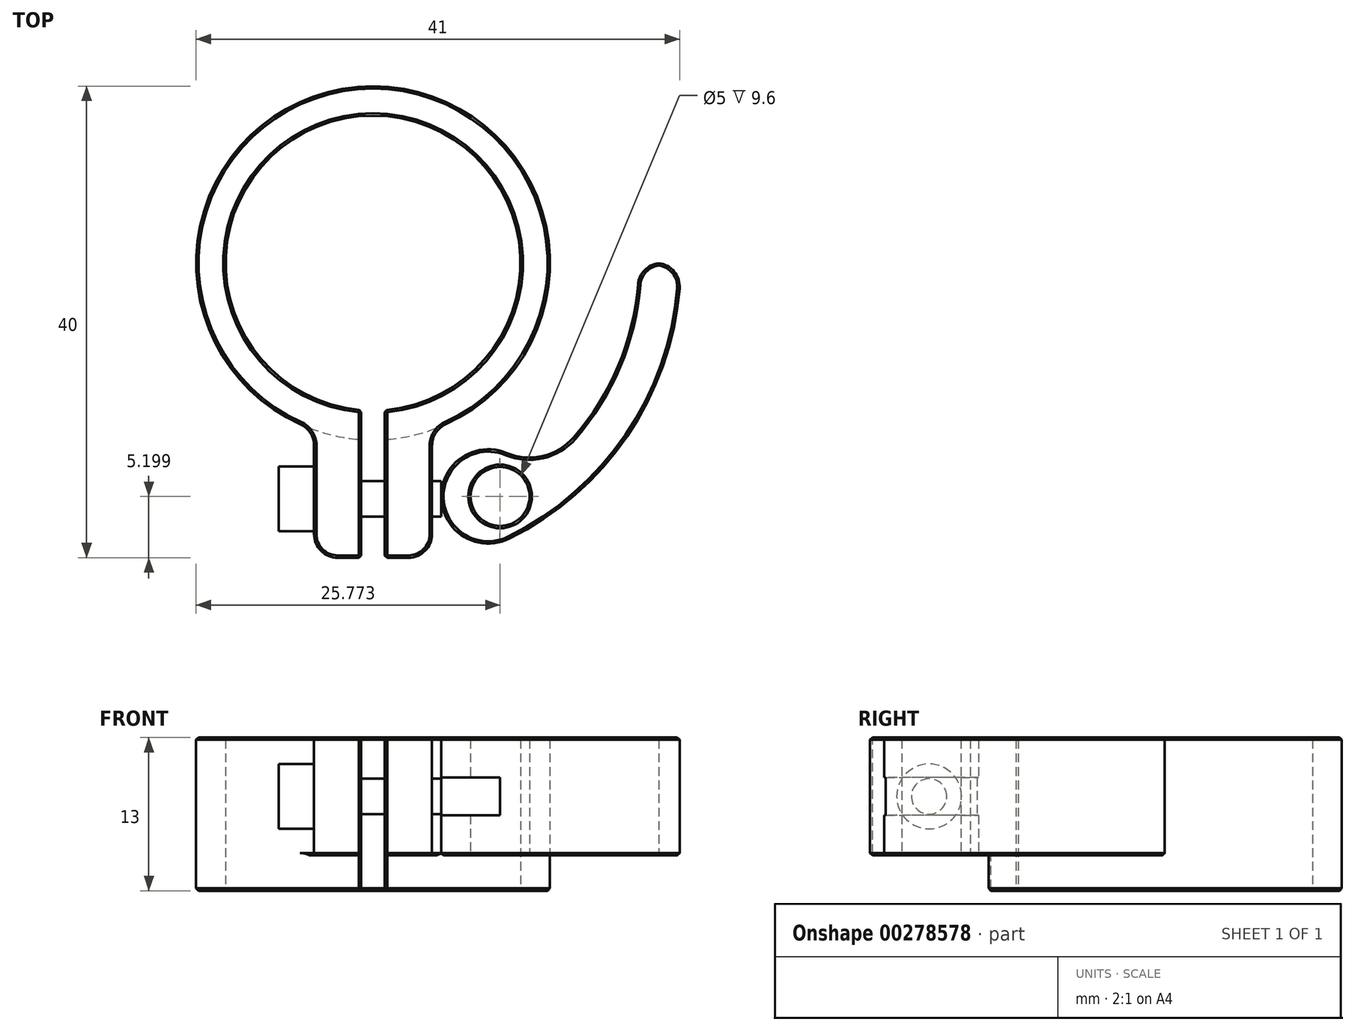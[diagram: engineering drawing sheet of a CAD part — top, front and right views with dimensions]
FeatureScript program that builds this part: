
annotation { "Feature Type Name" : "Feature", "Feature Type Description" : "" }
export const myFeature = defineFeature(function(context is Context, id is Id, definition is map)
    precondition{}
    {
        {
            var Q0;
            Q0=qCreatedBy(makeId("Top.planeOp"),FACE);
            var sketch = newSketch(context, id + "F0", { "sketchPlane" : qUnion([Q0])});
            skCircle(sketch, "E0", {"center": v(0, 0) * mm, "radius": 12.5 * mm});
            skCircle(sketch, "E1", {"center": v(0, 0) * mm, "radius": 15 * mm});
            skLineSegment(sketch, "E2.bottom", {"start": v(5, -25) * mm, "end": v(-5, -25) * mm});
            skLineSegment(sketch, "E2.top", {"start": v(5, 0) * mm, "end": v(-5, 0) * mm});
            skLineSegment(sketch, "E2.left", {"start": v(5, -25) * mm, "end": v(5, 0) * mm});
            skLineSegment(sketch, "E2.right", {"start": v(-5, -25) * mm, "end": v(-5, 0) * mm});
            skPoint(sketch, "E2.middle", {"position": v(0, -12.5) * mm});
            skLineSegment(sketch, "E3.bottom", {"start": v(1, -33.33) * mm, "end": v(-1, -33.33) * mm});
            skLineSegment(sketch, "E3.top", {"start": v(1, 8.32) * mm, "end": v(-1, 8.32) * mm});
            skLineSegment(sketch, "E3.left", {"start": v(1, -33.33) * mm, "end": v(1, 8.32) * mm});
            skLineSegment(sketch, "E3.right", {"start": v(-1, -33.33) * mm, "end": v(-1, 8.32) * mm});
            skSolve(sketch);
        }
        {
            var Q0;
            {var subQ0=sQuery(id+"F0.wireOp",EDGE,"E2.right");var subQ1=sQuery(id+"F0.wireOp",EDGE,"E0");var subQ2=makeQuery(id+"F0.imprint","INTERSECT",VERTEX,{"derivedFrom":[subQ1,subQ0]});Q0=makeQuery(id+"F0.imprint","IMPRINT",FACE,{"disambiguationData":[TD([[makeQuery(id+"F0.imprint","IMPRINT",EDGE,{"disambiguationData":[TD([[subQ2,1.0]])],"derivedFrom":subQ1}),-1.0]])]});}
            var Q1;
            {var subQ0=sQuery(id+"F0.wireOp",EDGE,"E2.left");var subQ1=sQuery(id+"F0.wireOp",EDGE,"E1");var subQ2=makeQuery(id+"F0.imprint","INTERSECT",VERTEX,{"derivedFrom":[subQ1,subQ0]});Q1=makeQuery(id+"F0.imprint","IMPRINT",FACE,{"disambiguationData":[TD([[makeQuery(id+"F0.imprint","IMPRINT",EDGE,{"disambiguationData":[TD([[subQ2,1.0]])],"derivedFrom":subQ1}),-1.0]])]});}
            var Q2;
            {var subQ0=sQuery(id+"F0.wireOp",EDGE,"E2.right");var subQ1=sQuery(id+"F0.wireOp",EDGE,"E1");var subQ2=makeQuery(id+"F0.imprint","INTERSECT",VERTEX,{"derivedFrom":[subQ1,subQ0]});Q2=makeQuery(id+"F0.imprint","IMPRINT",FACE,{"disambiguationData":[TD([[makeQuery(id+"F0.imprint","IMPRINT",EDGE,{"disambiguationData":[TD([[subQ2,-1.0]])],"derivedFrom":subQ1}),-1.0]])]});}
            var Q3;
            {var subQ0=sQuery(id+"F0.wireOp",EDGE,"E3.right");var subQ1=sQuery(id+"F0.wireOp",EDGE,"E0");var subQ2=makeQuery(id+"F0.imprint","INTERSECT",VERTEX,{"derivedFrom":[subQ1,subQ0]});Q3=makeQuery(id+"F0.imprint","IMPRINT",FACE,{"disambiguationData":[TD([[makeQuery(id+"F0.imprint","IMPRINT",EDGE,{"disambiguationData":[TD([[subQ2,1.0]])],"derivedFrom":subQ1}),-1.0]])]});}
            var Q4;
            {var subQ0=sQuery(id+"F0.wireOp",EDGE,"E3.left");var subQ1=sQuery(id+"F0.wireOp",EDGE,"E0");var subQ2=makeQuery(id+"F0.imprint","INTERSECT",VERTEX,{"derivedFrom":[subQ1,subQ0]});Q4=makeQuery(id+"F0.imprint","IMPRINT",FACE,{"disambiguationData":[TD([[makeQuery(id+"F0.imprint","IMPRINT",EDGE,{"disambiguationData":[TD([[subQ2,-1.0]])],"derivedFrom":subQ1}),-1.0]])]});}
            extrude(context, id + "F1", {"entities" : qUnion([Q0, Q1, Q2, Q3, Q4]), "depth" : 5 * mm, "hasSecondDirection" : true, "secondDirectionOppositeDirection" : true, "secondDirectionDepth" : 5 * mm});
        }
        {
            var Q0;
            {var subQ0=sQuery(id+"F0.wireOp",EDGE,"E2.right");var subQ1=sQuery(id+"F0.wireOp",EDGE,"E0");var subQ2=makeQuery(id+"F0.imprint","INTERSECT",VERTEX,{"derivedFrom":[subQ1,subQ0]});Q0=makeQuery(id+"F0.imprint","IMPRINT",FACE,{"disambiguationData":[TD([[makeQuery(id+"F0.imprint","IMPRINT",EDGE,{"disambiguationData":[TD([[subQ2,1.0]])],"derivedFrom":subQ1}),-1.0]])]});}
            var Q1;
            Q1=makeQuery(id+"F1.opExtrude","CAP_FACE",FACE,{"disambiguationData":[OSD([sQuery(id+"F0.wireOp",EDGE,"E0"),sQuery(id+"F0.wireOp",EDGE,"E1"),sQuery(id+"F0.wireOp",EDGE,"E2.bottom"),sQuery(id+"F0.wireOp",EDGE,"E2.left"),sQuery(id+"F0.wireOp",EDGE,"E2.right"),sQuery(id+"F0.wireOp",EDGE,"E3.left"),sQuery(id+"F0.wireOp",EDGE,"E3.right")])],"isStart":false});
            var Q2;
            {var subQ0=sQuery(id+"F0.wireOp",EDGE,"E3.right");var subQ1=sQuery(id+"F0.wireOp",EDGE,"E0");var subQ2=makeQuery(id+"F0.imprint","INTERSECT",VERTEX,{"derivedFrom":[subQ1,subQ0]});Q2=makeQuery(id+"F0.imprint","IMPRINT",FACE,{"disambiguationData":[TD([[makeQuery(id+"F0.imprint","IMPRINT",EDGE,{"disambiguationData":[TD([[subQ2,1.0]])],"derivedFrom":subQ1}),-1.0]])]});}
            var Q3;
            {var subQ0=sQuery(id+"F0.wireOp",EDGE,"E3.left");var subQ1=sQuery(id+"F0.wireOp",EDGE,"E0");var subQ2=makeQuery(id+"F0.imprint","INTERSECT",VERTEX,{"derivedFrom":[subQ1,subQ0]});Q3=makeQuery(id+"F0.imprint","IMPRINT",FACE,{"disambiguationData":[TD([[makeQuery(id+"F0.imprint","IMPRINT",EDGE,{"disambiguationData":[TD([[subQ2,-1.0]])],"derivedFrom":subQ1}),-1.0]])]});}
            extrude(context, id + "F2", {"entities" : qUnion([Q0, Q1, Q2, Q3]), "operationType" : NewBodyOperationType.ADD, "depth" : -8 * mm});
        }
        {
            var Q0;
            Q0=makeQuery(id+"F1.opExtrude","SWEPT_EDGE",EDGE,{"disambiguationData":[OSD([sQuery(id+"F0.wireOp",EDGE,"E1"),sQuery(id+"F0.wireOp",EDGE,"E2.right")])]});
            var Q1;
            Q1=makeQuery(id+"F1.opExtrude","SWEPT_EDGE",EDGE,{"disambiguationData":[OSD([sQuery(id+"F0.wireOp",EDGE,"E1"),sQuery(id+"F0.wireOp",EDGE,"E2.left")])]});
            var Q2;
            Q2=makeQuery(id+"F1.opExtrude","SWEPT_EDGE",EDGE,{"disambiguationData":[OSD([sQuery(id+"F0.wireOp",EDGE,"E2.bottom"),sQuery(id+"F0.wireOp",EDGE,"E2.right")])]});
            var Q3;
            Q3=makeQuery(id+"F1.opExtrude","SWEPT_EDGE",EDGE,{"disambiguationData":[OSD([sQuery(id+"F0.wireOp",EDGE,"E2.bottom"),sQuery(id+"F0.wireOp",EDGE,"E2.left")])]});
            fillet(context, id + "F3", {"entities" : qUnion([Q0, Q1, Q2, Q3]), "radius" : 2 * mm, "tangentPropagation" : true, "allowEdgeOverflow" : false});
        }
        {
            var Q0;
            Q0=makeQuery(id+"F1.opExtrude","CAP_EDGE",EDGE,{"disambiguationData":[OSD([sQuery(id+"F0.wireOp",EDGE,"E0")])],"isStart":false});
            var Q1;
            Q1=makeQuery(id+"F1.opExtrude","CAP_EDGE",EDGE,{"disambiguationData":[OSD([sQuery(id+"F0.wireOp",EDGE,"E1")])],"isStart":false});
            var Q2;
            Q2=makeQuery(id+"F1.opExtrude","CAP_EDGE",EDGE,{"disambiguationData":[OSD([sQuery(id+"F0.wireOp",EDGE,"E2.right")])],"isStart":false});
            var Q3;
            Q3=makeQuery(id+"F1.opExtrude","CAP_EDGE",EDGE,{"disambiguationData":[OSD([sQuery(id+"F0.wireOp",EDGE,"E2.left")])],"isStart":false});
            var Q4;
            Q4=makeQuery(id+"F1.opExtrude","CAP_EDGE",EDGE,{"disambiguationData":[OSD([sQuery(id+"F0.wireOp",EDGE,"E3.right")])],"isStart":false});
            var Q5;
            Q5=makeQuery(id+"F1.opExtrude","CAP_EDGE",EDGE,{"disambiguationData":[OSD([sQuery(id+"F0.wireOp",EDGE,"E3.left")])],"isStart":false});
            var Q6;
            {var subQ0=sQuery(id+"F0.wireOp",EDGE,"E3.left");var subQ1=sQuery(id+"F0.wireOp",EDGE,"E0");Q6=makeQuery(id+"F2.boolean.opBoolean","MERGE",EDGE,{"derivedFrom":[makeQuery(id+"F1.opExtrude","SWEPT_EDGE",EDGE,{"disambiguationData":[OSD([subQ1,subQ0])]}),makeQuery(id+"F2.opExtrude","SWEPT_EDGE",EDGE,{"disambiguationData":[OSD([subQ1,subQ0]),TDD([makeQuery(id+"F0.imprint","INTERSECT",VERTEX,{"derivedFrom":[subQ1,subQ0]})])]}),makeQuery(id+"F2.opExtrude","SWEPT_EDGE",EDGE,{"disambiguationData":[OSD([subQ1,subQ0]),TDD([makeQuery(id+"F1.opExtrude","CAP_VERTEX",VERTEX,{"disambiguationData":[OSD([subQ1,subQ0])],"isStart":false})])]})]});}
            var Q7;
            {var subQ0=sQuery(id+"F0.wireOp",EDGE,"E0");var subQ1=makeQuery(id+"F0.imprint","INTERSECT",VERTEX,{"derivedFrom":[subQ0,sQuery(id+"F0.wireOp",EDGE,"E2.right")]});Q7=makeQuery(id+"F2.boolean.opBoolean","MERGE",FACE,{"derivedFrom":[makeQuery(id+"F1.opExtrude","SWEPT_FACE",FACE,{"disambiguationData":[OSD([subQ0])]}),makeQuery(id+"F2.opExtrude","SWEPT_FACE",FACE,{"disambiguationData":[OSD([subQ0]),TDD([makeQuery(id+"F0.imprint","IMPRINT",EDGE,{"disambiguationData":[TD([[makeQuery(id+"F0.imprint","INTERSECT",VERTEX,{"derivedFrom":[subQ0,sQuery(id+"F0.wireOp",EDGE,"E3.right")]}),1.0]])],"derivedFrom":subQ0}),makeQuery(id+"F0.imprint","IMPRINT",EDGE,{"disambiguationData":[TD([[makeQuery(id+"F0.imprint","INTERSECT",VERTEX,{"derivedFrom":[subQ0,sQuery(id+"F0.wireOp",EDGE,"E3.left")]}),-1.0]])],"derivedFrom":subQ0}),makeQuery(id+"F0.imprint","IMPRINT",EDGE,{"disambiguationData":[TD([[subQ1,1.0]])],"derivedFrom":subQ0})])]}),makeQuery(id+"F2.opExtrude","SWEPT_FACE",FACE,{"disambiguationData":[OSD([subQ0]),TDD([makeQuery(id+"F1.opExtrude","CAP_EDGE",EDGE,{"disambiguationData":[OSD([subQ0])],"isStart":false})])]})]});}
            var Q8;
            Q8=makeQuery(id+"F1.opExtrude","CAP_EDGE",EDGE,{"disambiguationData":[OSD([sQuery(id+"F0.wireOp",EDGE,"E3.left")])],"isStart":true});
            var Q9;
            Q9=makeQuery(id+"F1.opExtrude","SWEPT_EDGE",EDGE,{"disambiguationData":[OSD([sQuery(id+"F0.wireOp",EDGE,"E2.bottom"),sQuery(id+"F0.wireOp",EDGE,"E3.left")])]});
            var Q10;
            Q10=makeQuery(id+"F1.opExtrude","SWEPT_EDGE",EDGE,{"disambiguationData":[OSD([sQuery(id+"F0.wireOp",EDGE,"E2.bottom"),sQuery(id+"F0.wireOp",EDGE,"E3.right")])]});
            var Q11;
            Q11=makeQuery(id+"F1.opExtrude","CAP_EDGE",EDGE,{"disambiguationData":[OSD([sQuery(id+"F0.wireOp",EDGE,"E3.right")])],"isStart":true});
            var Q12;
            {var subQ0=sQuery(id+"F0.wireOp",EDGE,"E1");var subQ1=makeQuery(id+"F0.imprint","INTERSECT",VERTEX,{"derivedFrom":[subQ0,sQuery(id+"F0.wireOp",EDGE,"E2.right")]});var subQ2=makeQuery(id+"F0.imprint","INTERSECT",VERTEX,{"derivedFrom":[subQ0,sQuery(id+"F0.wireOp",EDGE,"E2.left")]});Q12=makeQuery(id+"F2.opExtrude","CAP_EDGE",EDGE,{"disambiguationData":[OSD([subQ0]),TDD([makeQuery(id+"F0.imprint","IMPRINT",EDGE,{"disambiguationData":[TD([[subQ1,-1.0]])],"derivedFrom":subQ0}),makeQuery(id+"F0.imprint","IMPRINT",EDGE,{"disambiguationData":[TD([[subQ2,1.0]])],"derivedFrom":subQ0}),makeQuery(id+"F0.imprint","IMPRINT",EDGE,{"disambiguationData":[TD([[subQ1,1.0]])],"derivedFrom":subQ0})])],"isStart":false});}
            var Q13;
            Q13=makeQuery(id+"F2.opExtrude","SWEPT_EDGE",EDGE,{"disambiguationData":[OSD([sQuery(id+"F0.wireOp",EDGE,"E1"),sQuery(id+"F0.wireOp",EDGE,"E3.left")])]});
            var Q14;
            Q14=makeQuery(id+"F2.opExtrude","SWEPT_EDGE",EDGE,{"disambiguationData":[OSD([sQuery(id+"F0.wireOp",EDGE,"E1"),sQuery(id+"F0.wireOp",EDGE,"E3.right")])]});
            var Q15;
            {var subQ0=sQuery(id+"F0.wireOp",EDGE,"E3.left");Q15=makeQuery(id+"F2.opExtrude","CAP_EDGE",EDGE,{"disambiguationData":[OSD([subQ0]),TDD([makeQuery(id+"F0.imprint","IMPRINT",EDGE,{"disambiguationData":[TD([[makeQuery(id+"F0.imprint","INTERSECT",VERTEX,{"derivedFrom":[sQuery(id+"F0.wireOp",EDGE,"E0"),subQ0]}),1.0]])],"derivedFrom":subQ0})])],"isStart":false});}
            var Q16;
            {var subQ0=sQuery(id+"F0.wireOp",EDGE,"E3.right");Q16=makeQuery(id+"F2.opExtrude","CAP_EDGE",EDGE,{"disambiguationData":[OSD([subQ0]),TDD([makeQuery(id+"F0.imprint","IMPRINT",EDGE,{"disambiguationData":[TD([[makeQuery(id+"F0.imprint","INTERSECT",VERTEX,{"derivedFrom":[sQuery(id+"F0.wireOp",EDGE,"E0"),subQ0]}),1.0]])],"derivedFrom":subQ0})])],"isStart":false});}
            var Q17;
            Q17=makeQuery(id+"F1.opExtrude","CAP_EDGE",EDGE,{"disambiguationData":[OSD([sQuery(id+"F0.wireOp",EDGE,"E2.right")])],"isStart":true});
            var Q18;
            Q18=makeQuery(id+"F1.opExtrude","CAP_EDGE",EDGE,{"disambiguationData":[OSD([sQuery(id+"F0.wireOp",EDGE,"E2.left")])],"isStart":true});
            chamfer(context, id + "F4", {"entities" : qUnion([Q0, Q1, Q2, Q3, Q4, Q5, Q6, Q7, Q8, Q9, Q10, Q11, Q12, Q13, Q14, Q15, Q16, Q17, Q18]), "width" : 0.2 * mm, "tangentPropagation" : true});
        }
        {
            var Q0;
            Q0=makeQuery(id+"F1.opExtrude","SWEPT_FACE",FACE,{"disambiguationData":[OSD([sQuery(id+"F0.wireOp",EDGE,"E2.right")])]});
            var sketch = newSketch(context, id + "F5", { "sketchPlane" : qUnion([Q0])});
            skCircle(sketch, "E4", {"center": v(20, 0) * mm, "radius": 1.5 * mm});
            skCircle(sketch, "E5", {"center": v(20, 0) * mm, "radius": 2.75 * mm});
            skSolve(sketch);
        }
        {
            var Q0;
            Q0=makeQuery(id+"F5.imprint","IMPRINT",FACE,{"disambiguationData":[TD([[makeQuery(id+"F5.imprint","IMPRINT",EDGE,{"derivedFrom":sQuery(id+"F5.wireOp",EDGE,"E4")}),1.0]])]});
            extrude(context, id + "F6", {"entities" : qUnion([Q0]), "operationType" : NewBodyOperationType.REMOVE, "oppositeDirection" : true, "depth" : 25 * mm});
        }
        {
            var Q0;
            Q0=makeQuery(id+"F5.imprint","IMPRINT",FACE,{"disambiguationData":[TD([[makeQuery(id+"F5.imprint","IMPRINT",EDGE,{"derivedFrom":sQuery(id+"F5.wireOp",EDGE,"E4")}),-1.0]])]});
            var Q1;
            Q1=makeQuery(id+"F5.imprint","IMPRINT",FACE,{"disambiguationData":[TD([[makeQuery(id+"F5.imprint","IMPRINT",EDGE,{"derivedFrom":sQuery(id+"F5.wireOp",EDGE,"E4")}),1.0]])]});
            extrude(context, id + "F7", {"entities" : qUnion([Q0, Q1]), "depth" : 3 * mm});
        }
        {
            var Q0;
            Q0=makeQuery(id+"F5.imprint","IMPRINT",FACE,{"disambiguationData":[TD([[makeQuery(id+"F5.imprint","IMPRINT",EDGE,{"derivedFrom":sQuery(id+"F5.wireOp",EDGE,"E4")}),1.0]])]});
            extrude(context, id + "F8", {"entities" : qUnion([Q0]), "operationType" : NewBodyOperationType.ADD, "oppositeDirection" : true, "depth" : 14.67 * mm});
        }
        {
            var Q0;
            Q0=qCreatedBy(makeId("Top.planeOp"),FACE);
            var sketch = newSketch(context, id + "F9", { "sketchPlane" : qUnion([Q0])});
            skCircle(sketch, "E6", {"center": v(10.77, -19.8) * mm, "radius": 2.5 * mm});
            skCircle(sketch, "E7", {"center": v(9.77, -19.8) * mm, "radius": 4 * mm});
            skCircle(sketch, "E8", {"center": v(0, 0) * mm, "radius": 26.08 * mm});
            skCircle(sketch, "E9", {"center": v(0, 0) * mm, "radius": 22.54 * mm});
            skLineSegment(sketch, "E10", {"start": v(22.54, 0) * mm, "end": v(26.08, 0) * mm});
            skLineSegment(sketch, "E11.bottom", {"start": v(5.77, -24.1) * mm, "end": v(10.77, -24.1) * mm});
            skLineSegment(sketch, "E11.top", {"start": v(5.77, -14.58) * mm, "end": v(10.77, -14.58) * mm});
            skLineSegment(sketch, "E11.left", {"start": v(5.77, -24.1) * mm, "end": v(5.77, -14.58) * mm});
            skLineSegment(sketch, "E11.right", {"start": v(10.77, -24.1) * mm, "end": v(10.77, -14.58) * mm});
            skSolve(sketch);
        }
        {
            var Q0;
            {var subQ2=sQuery(id+"F9.wireOp",EDGE,"E9");var subQ4=sQuery(id+"F9.wireOp",EDGE,"E6");var subQ5=makeQuery(id+"F9.imprint","INTERSECT",VERTEX,{"disambiguationData":[OD(0.0)],"derivedFrom":[subQ4,subQ2]});Q0=makeQuery(id+"F9.imprint","IMPRINT",FACE,{"disambiguationData":[TD([[makeQuery(id+"F9.imprint","IMPRINT",EDGE,{"disambiguationData":[TD([[subQ5,-1.0]])],"derivedFrom":subQ4}),-1.0]])]});}
            var Q1;
            {var subQ0=sQuery(id+"F9.wireOp",EDGE,"E9");var subQ1=sQuery(id+"F9.wireOp",EDGE,"E6");var subQ2=makeQuery(id+"F9.imprint","INTERSECT",VERTEX,{"disambiguationData":[OD(0.0)],"derivedFrom":[subQ1,subQ0]});Q1=makeQuery(id+"F9.imprint","IMPRINT",FACE,{"disambiguationData":[TD([[makeQuery(id+"F9.imprint","IMPRINT",EDGE,{"disambiguationData":[TD([[subQ2,1.0]])],"derivedFrom":subQ1}),-1.0]])]});}
            var Q2;
            {var subQ5=sQuery(id+"F9.wireOp",EDGE,"E10");Q2=makeQuery(id+"F9.imprint","IMPRINT",FACE,{"disambiguationData":[TD([[makeQuery(id+"F9.imprint","IMPRINT",EDGE,{"derivedFrom":subQ5}),-1.0]])]});}
            var Q3;
            {var subQ0=sQuery(id+"F9.wireOp",EDGE,"9b3e7e2a-e51d-4acb-ae69-ad82b6e70bec.right");var subQ1=sQuery(id+"F9.wireOp",EDGE,"E6");var subQ2=makeQuery(id+"F9.imprint","INTERSECT",VERTEX,{"disambiguationData":[OD(0.0)],"derivedFrom":[subQ1,subQ0]});Q3=makeQuery(id+"F9.imprint","IMPRINT",FACE,{"disambiguationData":[TD([[makeQuery(id+"F9.imprint","IMPRINT",EDGE,{"disambiguationData":[TD([[subQ2,-1.0]])],"derivedFrom":subQ1}),-1.0]])]});}
            var Q4;
            {var subQ5=sQuery(id+"F9.wireOp",EDGE,"E6");var subQ7=sQuery(id+"F9.wireOp",EDGE,"E11.right");var subQ9=makeQuery(id+"F9.imprint","INTERSECT",VERTEX,{"disambiguationData":[OD(0.0)],"derivedFrom":[subQ5,subQ7]});Q4=makeQuery(id+"F9.imprint","IMPRINT",FACE,{"disambiguationData":[TD([[makeQuery(id+"F9.imprint","IMPRINT",EDGE,{"disambiguationData":[TD([[subQ9,-1.0]])],"derivedFrom":subQ5}),-1.0]])]});}
            var Q5;
            {var subQ0=sQuery(id+"F9.wireOp",EDGE,"E9");var subQ1=sQuery(id+"F9.wireOp",EDGE,"E7");var subQ2=makeQuery(id+"F9.imprint","INTERSECT",VERTEX,{"disambiguationData":[OD(1.0)],"derivedFrom":[subQ1,subQ0]});Q5=makeQuery(id+"F9.imprint","IMPRINT",FACE,{"disambiguationData":[TD([[makeQuery(id+"F9.imprint","IMPRINT",EDGE,{"disambiguationData":[TD([[subQ2,-1.0]])],"derivedFrom":subQ1}),1.0]])]});}
            var Q6;
            {var subQ5=sQuery(id+"F9.wireOp",EDGE,"E9");var subQ7=sQuery(id+"F9.wireOp",EDGE,"E6");var subQ8=makeQuery(id+"F9.imprint","INTERSECT",VERTEX,{"disambiguationData":[OD(1.0)],"derivedFrom":[subQ7,subQ5]});Q6=makeQuery(id+"F9.imprint","IMPRINT",FACE,{"disambiguationData":[TD([[makeQuery(id+"F9.imprint","IMPRINT",EDGE,{"disambiguationData":[TD([[subQ8,-1.0]])],"derivedFrom":subQ7}),-1.0]])]});}
            var Q7;
            {var subQ0=sQuery(id+"F9.wireOp",EDGE,"E11.left");var subQ1=sQuery(id+"F9.wireOp",EDGE,"E7");var subQ2=makeQuery(id+"F9.imprint","INTERSECT",VERTEX,{"disambiguationData":[OD(0.0)],"derivedFrom":[subQ1,subQ0]});Q7=makeQuery(id+"F9.imprint","IMPRINT",FACE,{"disambiguationData":[TD([[makeQuery(id+"F9.imprint","IMPRINT",EDGE,{"disambiguationData":[TD([[subQ2,-1.0]])],"derivedFrom":subQ1}),1.0]])]});}
            extrude(context, id + "F10", {"entities" : qUnion([Q0, Q1, Q2, Q3, Q4, Q5, Q6, Q7]), "depth" : 5 * mm, "hasSecondDirection" : true, "secondDirectionOppositeDirection" : true, "secondDirectionDepth" : 5 * mm});
        }
        {
            var Q0;
            Q0=makeQuery(id+"F10.opExtrude","SWEPT_EDGE",EDGE,{"disambiguationData":[OSD([sQuery(id+"F9.wireOp",EDGE,"E9"),sQuery(id+"F9.wireOp",EDGE,"E10")])]});
            var Q1;
            Q1=makeQuery(id+"F10.opExtrude","SWEPT_EDGE",EDGE,{"disambiguationData":[OSD([sQuery(id+"F9.wireOp",EDGE,"E8"),sQuery(id+"F9.wireOp",EDGE,"E10")])]});
            fillet(context, id + "F11", {"entities" : qUnion([Q0, Q1]), "radius" : 2 * mm, "tangentPropagation" : true, "allowEdgeOverflow" : false});
        }
        {
            var Q0;
            Q0=makeQuery(id+"F10.opExtrude","SWEPT_EDGE",EDGE,{"disambiguationData":[OSD([sQuery(id+"F9.wireOp",EDGE,"E7"),sQuery(id+"F9.wireOp",EDGE,"E9")])]});
            fillet(context, id + "F12", {"entities" : qUnion([Q0]), "radius" : 5 * mm, "tangentPropagation" : true, "allowEdgeOverflow" : false});
        }
        {
            var Q0;
            Q0=makeQuery(id+"F10.opExtrude","CAP_EDGE",EDGE,{"disambiguationData":[OSD([sQuery(id+"F9.wireOp",EDGE,"E8")])],"isStart":false});
            var Q1;
            Q1=makeQuery(id+"F10.opExtrude","CAP_EDGE",EDGE,{"disambiguationData":[OSD([sQuery(id+"F9.wireOp",EDGE,"E8")])],"isStart":true});
            var Q2;
            Q2=makeQuery(id+"F10.opExtrude","CAP_FACE",FACE,{"disambiguationData":[OSD([sQuery(id+"F9.wireOp",EDGE,"E6"),sQuery(id+"F9.wireOp",EDGE,"E7"),sQuery(id+"F9.wireOp",EDGE,"E8"),sQuery(id+"F9.wireOp",EDGE,"E9"),sQuery(id+"F9.wireOp",EDGE,"E10")])],"isStart":true});
            var Q3;
            Q3=makeQuery(id+"F10.opExtrude","CAP_EDGE",EDGE,{"disambiguationData":[OSD([sQuery(id+"F9.wireOp",EDGE,"E6")])],"isStart":false});
            chamfer(context, id + "F13", {"entities" : qUnion([Q0, Q1, Q2, Q3]), "width" : 0.2 * mm, "tangentPropagation" : true});
        }
        {
            var Q0;
            {var subQ5=sQuery(id+"F9.wireOp",EDGE,"E9");var subQ7=sQuery(id+"F9.wireOp",EDGE,"E6");var subQ8=makeQuery(id+"F9.imprint","INTERSECT",VERTEX,{"disambiguationData":[OD(1.0)],"derivedFrom":[subQ7,subQ5]});Q0=makeQuery(id+"F9.imprint","IMPRINT",FACE,{"disambiguationData":[TD([[makeQuery(id+"F9.imprint","IMPRINT",EDGE,{"disambiguationData":[TD([[subQ8,-1.0]])],"derivedFrom":subQ7}),-1.0]])]});}
            var Q1;
            {var subQ0=sQuery(id+"F9.wireOp",EDGE,"E9");var subQ1=sQuery(id+"F9.wireOp",EDGE,"E6");var subQ2=makeQuery(id+"F9.imprint","INTERSECT",VERTEX,{"disambiguationData":[OD(1.0)],"derivedFrom":[subQ1,subQ0]});Q1=makeQuery(id+"F9.imprint","IMPRINT",FACE,{"disambiguationData":[TD([[makeQuery(id+"F9.imprint","IMPRINT",EDGE,{"disambiguationData":[TD([[subQ2,-1.0]])],"derivedFrom":subQ1}),1.0]])]});}
            var Q2;
            {var subQ0=sQuery(id+"F9.wireOp",EDGE,"E11.right");var subQ1=sQuery(id+"F9.wireOp",EDGE,"E6");var subQ2=makeQuery(id+"F9.imprint","INTERSECT",VERTEX,{"disambiguationData":[OD(0.0)],"derivedFrom":[subQ1,subQ0]});Q2=makeQuery(id+"F9.imprint","IMPRINT",FACE,{"disambiguationData":[TD([[makeQuery(id+"F9.imprint","IMPRINT",EDGE,{"disambiguationData":[TD([[subQ2,-1.0]])],"derivedFrom":subQ1}),1.0]])]});}
            var Q3;
            {var subQ5=sQuery(id+"F9.wireOp",EDGE,"E6");var subQ7=sQuery(id+"F9.wireOp",EDGE,"E11.right");var subQ9=makeQuery(id+"F9.imprint","INTERSECT",VERTEX,{"disambiguationData":[OD(0.0)],"derivedFrom":[subQ5,subQ7]});Q3=makeQuery(id+"F9.imprint","IMPRINT",FACE,{"disambiguationData":[TD([[makeQuery(id+"F9.imprint","IMPRINT",EDGE,{"disambiguationData":[TD([[subQ9,-1.0]])],"derivedFrom":subQ5}),-1.0]])]});}
            var Q4;
            {var subQ0=sQuery(id+"F9.wireOp",EDGE,"E11.left");var subQ3=sQuery(id+"F9.wireOp",EDGE,"E7");var subQ4=makeQuery(id+"F9.imprint","INTERSECT",VERTEX,{"disambiguationData":[OD(1.0)],"derivedFrom":[subQ3,subQ0]});Q4=makeQuery(id+"F9.imprint","IMPRINT",FACE,{"disambiguationData":[TD([[makeQuery(id+"F9.imprint","IMPRINT",EDGE,{"disambiguationData":[TD([[subQ4,-1.0]])],"derivedFrom":subQ3}),-1.0]])]});}
            var Q5;
            {var subQ0=sQuery(id+"F9.wireOp",EDGE,"E11.bottom");var subQ1=sQuery(id+"F9.wireOp",EDGE,"E8");var subQ2=makeQuery(id+"F9.imprint","INTERSECT",VERTEX,{"derivedFrom":[subQ1,subQ0]});Q5=makeQuery(id+"F9.imprint","IMPRINT",FACE,{"disambiguationData":[TD([[makeQuery(id+"F9.imprint","IMPRINT",EDGE,{"disambiguationData":[TD([[subQ2,-1.0]])],"derivedFrom":subQ1}),-1.0]])]});}
            var Q6;
            {var subQ5=sQuery(id+"F9.wireOp",EDGE,"E11.top");Q6=makeQuery(id+"F9.imprint","IMPRINT",FACE,{"disambiguationData":[TD([[makeQuery(id+"F9.imprint","IMPRINT",EDGE,{"derivedFrom":subQ5}),-1.0]])]});}
            extrude(context, id + "F14", {"entities" : qUnion([Q0, Q1, Q2, Q3, Q4, Q5, Q6]), "operationType" : NewBodyOperationType.REMOVE, "oppositeDirection" : true, "depth" : 1.6 * mm, "hasSecondDirection" : true, "secondDirectionOppositeDirection" : true, "secondDirectionDepth" : -1.6 * mm});
        }
    });
